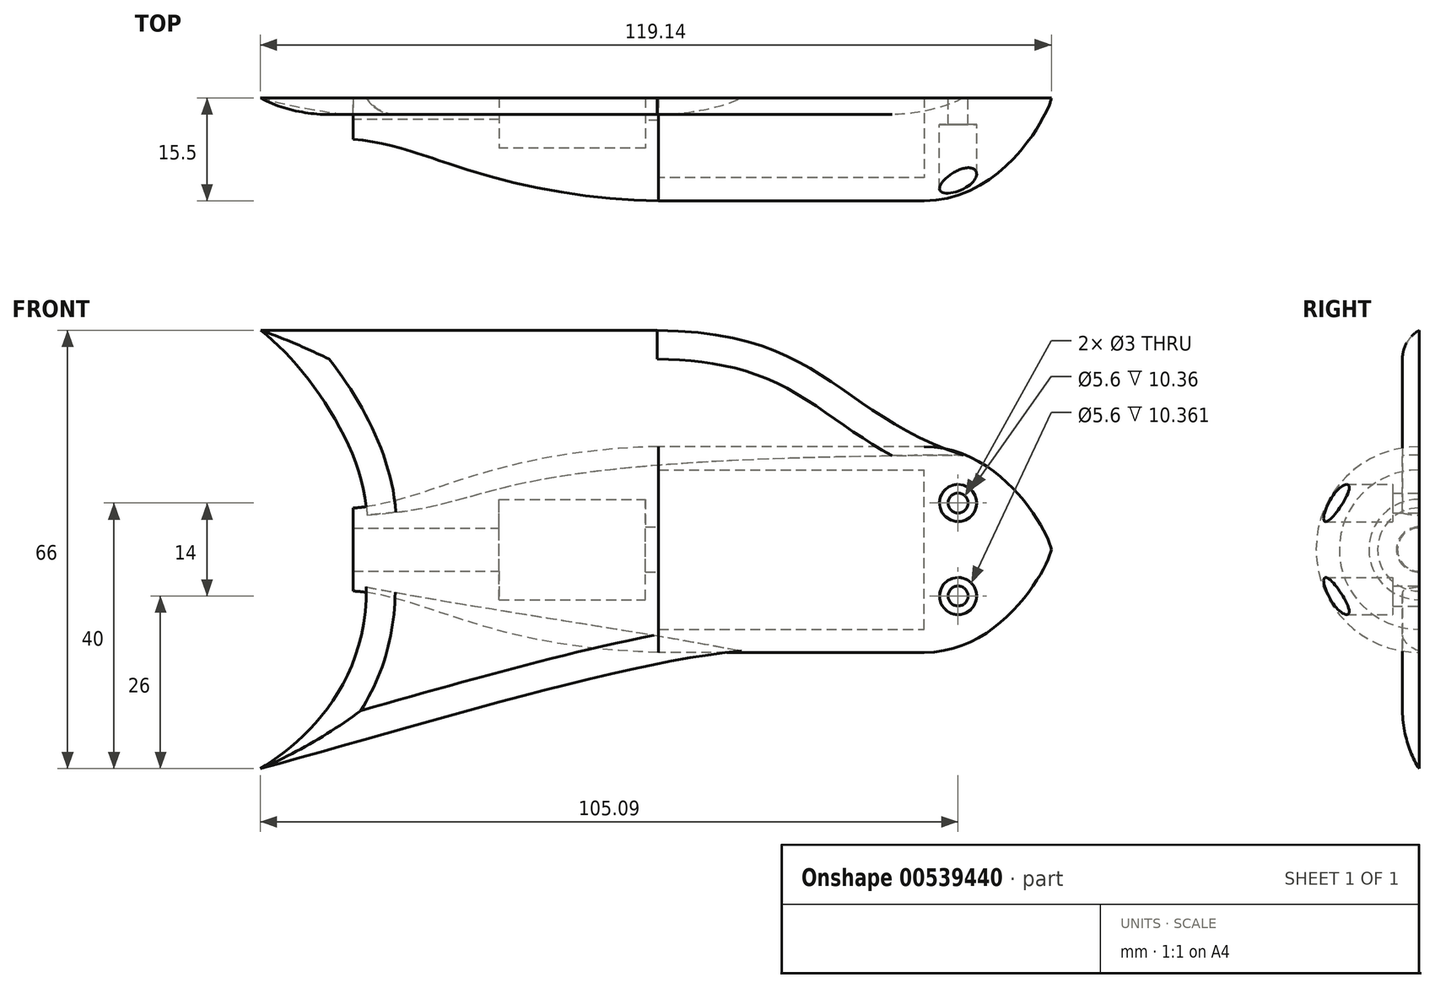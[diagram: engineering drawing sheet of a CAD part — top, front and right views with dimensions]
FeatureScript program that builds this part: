
annotation { "Feature Type Name" : "Feature", "Feature Type Description" : "" }
export const myFeature = defineFeature(function(context is Context, id is Id, definition is map)
    precondition{}
    {
        {
            var Q0;
            Q0=qCreatedBy(makeId("Front.planeOp"),FACE);
            var sketch = newSketch(context, id + "F0", { "sketchPlane" : qUnion([Q0])});
            skLineSegment(sketch, "E0", {"start": v(-75.09, 3.25) * mm, "end": v(-53.09, 3.25) * mm});
            skLineSegment(sketch, "E1", {"start": v(-53.09, 3.25) * mm, "end": v(-53.09, 7.55) * mm});
            skLineSegment(sketch, "E2", {"start": v(-53.09, 7.55) * mm, "end": v(-31.09, 7.55) * mm});
            skLineSegment(sketch, "E3", {"start": v(-31.09, 7.55) * mm, "end": v(-31.09, 3.4) * mm});
            skLineSegment(sketch, "E4", {"start": v(-31.09, 3.4) * mm, "end": v(-29.09, 3.4) * mm});
            skLineSegment(sketch, "E5", {"start": v(-29.09, 3.4) * mm, "end": v(-29.09, 12) * mm});
            skLineSegment(sketch, "E6", {"start": v(-29.09, 12) * mm, "end": v(10.91, 12) * mm});
            skLineSegment(sketch, "E7", {"start": v(10.91, 12) * mm, "end": v(10.91, 0) * mm});
            skLineSegment(sketch, "E8", {"start": v(10.91, 0) * mm, "end": v(30.05, 0) * mm});
            skLineSegment(sketch, "E9", {"start": v(-75.09, 6.25) * mm, "end": v(-75.09, 3.25) * mm});
            skLineSegment(sketch, "E10", {"start": v(10.91, 15.5) * mm, "end": v(-29.14, 15.5) * mm});
            skFitSpline(sketch, "E11", {"points": [v(30.05, 0) * mm, v(10.91, 15.5) * mm], "startDerivative": vector(-1.53, 7.93) * mm, "endDerivative": vector(-35.34, 0.06) * mm});
            skLineSegment(sketch, "E12", {"start": v(-31.09, 3.4) * mm, "end": v(-31.09, 0) * mm});
            skFitSpline(sketch, "E13", {"points": [v(-29.14, 15.5) * mm, v(-75.09, 6.25) * mm], "startDerivative": vector(-76.48, -1.84) * mm, "endDerivative": vector(-32.8, -2) * mm});
            skLineSegment(sketch, "E14", {"start": v(-53.09, 3.25) * mm, "end": v(-53.09, 0) * mm});
            skSolve(sketch);
        }
        {
            var Q0;
            Q0=makeQuery(id+"F0.imprint","IMPRINT",FACE,{"disambiguationData":[TD([[makeQuery(id+"F0.imprint","IMPRINT",EDGE,{"derivedFrom":sQuery(id+"F0.wireOp",EDGE,"E0")}),1.0]])]});
            var Q1;
            Q1=sQuery(id+"F0.wireOp",EDGE,"E8");
            revolve(context, id + "F1", {"entities" : qUnion([Q0]), "axis" : qUnion([Q1]), "revolveType" : RevolveType.ONE_DIRECTION, "angle" : 180 * degree});
        }
        {
            var Q0;
            Q0=qCreatedBy(makeId("Right.planeOp"),FACE);
            var sketch = newSketch(context, id + "F2", { "sketchPlane" : qUnion([Q0])});
            skLineSegment(sketch, "E15", {"start": v(-16.61, 2.8) * mm, "end": v(-4, 2.8) * mm});
            skLineSegment(sketch, "E16", {"start": v(-4, 2.8) * mm, "end": v(-4, 1.5) * mm});
            skLineSegment(sketch, "E17", {"start": v(-4, 1.5) * mm, "end": v(0, 1.5) * mm});
            skLineSegment(sketch, "E18", {"start": v(0, 1.5) * mm, "end": v(0, 0) * mm});
            skLineSegment(sketch, "E19", {"start": v(0, 0) * mm, "end": v(-16.61, 0) * mm});
            skLineSegment(sketch, "E20", {"start": v(-16.61, 2.8) * mm, "end": v(-16.61, 0) * mm});
            skSolve(sketch);
        }
        {
            var Q0;
            Q0=makeQuery(id+"F2.imprint","IMPRINT",FACE,{"disambiguationData":[TD([[makeQuery(id+"F2.imprint","IMPRINT",EDGE,{"derivedFrom":sQuery(id+"F2.wireOp",EDGE,"pKEryXh2-qbwp-OUbP-EK2V-zjAWTAb98PYZ")}),-1.0]])]});
            var Q1;
            Q1=makeQuery(id+"F2.imprint","IMPRINT",FACE,{"disambiguationData":[TD([[makeQuery(id+"F2.imprint","IMPRINT",EDGE,{"derivedFrom":sQuery(id+"F2.wireOp",EDGE,"E15")}),-1.0]])]});
            var Q2;
            Q2=sQuery(id+"F2.wireOp",EDGE,"E19");
            revolve(context, id + "F3", {"entities" : qUnion([Q0, Q1]), "axis" : qUnion([Q2]), "revolveType" : RevolveType.FULL});
        }
        {
            var Q0;
            Q0=makeQuery(id+"F3.opRevolve","SWEPT_BODY",BODY,{"disambiguationData":[OSD([sQuery(id+"F2.wireOp",EDGE,"E15"),sQuery(id+"F2.wireOp",EDGE,"E16"),sQuery(id+"F2.wireOp",EDGE,"E17"),sQuery(id+"F2.wireOp",EDGE,"E18"),sQuery(id+"F2.wireOp",EDGE,"E19"),sQuery(id+"F2.wireOp",EDGE,"E20")])]});
            transform(context, id + "F4", {"entities" : qUnion([Q0]), "transformType" : TransformType.TRANSLATION_3D, "dx" : 16 * mm, "dy" : 0 * mm, "dz" : 7 * mm, "makeCopy" : false});
        }
        {
            var Q0;
            Q0=makeQuery(id+"F3.opRevolve","SWEPT_BODY",BODY,{"disambiguationData":[OSD([sQuery(id+"F2.wireOp",EDGE,"E15"),sQuery(id+"F2.wireOp",EDGE,"E16"),sQuery(id+"F2.wireOp",EDGE,"E17"),sQuery(id+"F2.wireOp",EDGE,"E18"),sQuery(id+"F2.wireOp",EDGE,"E19"),sQuery(id+"F2.wireOp",EDGE,"E20")])]});
            transform(context, id + "F5", {"entities" : qUnion([Q0]), "transformType" : TransformType.TRANSLATION_3D, "dx" : 0 * mm, "dy" : 0 * mm, "dz" : -14 * mm, "makeCopy" : true});
        }
        {
            var Q0;
            Q0=makeQuery(id+"F3.opRevolve","SWEPT_BODY",BODY,{"disambiguationData":[OSD([sQuery(id+"F2.wireOp",EDGE,"E15"),sQuery(id+"F2.wireOp",EDGE,"E16"),sQuery(id+"F2.wireOp",EDGE,"E17"),sQuery(id+"F2.wireOp",EDGE,"E18"),sQuery(id+"F2.wireOp",EDGE,"E19"),sQuery(id+"F2.wireOp",EDGE,"E20")])]});
            var Q1;
            Q1=makeQuery(id+"F1.opRevolve","SWEPT_BODY",BODY,{"disambiguationData":[OSD([sQuery(id+"F0.wireOp",EDGE,"E0"),sQuery(id+"F0.wireOp",EDGE,"E1"),sQuery(id+"F0.wireOp",EDGE,"E2"),sQuery(id+"F0.wireOp",EDGE,"E3"),sQuery(id+"F0.wireOp",EDGE,"E4"),sQuery(id+"F0.wireOp",EDGE,"E5"),sQuery(id+"F0.wireOp",EDGE,"E6"),sQuery(id+"F0.wireOp",EDGE,"E7"),sQuery(id+"F0.wireOp",EDGE,"E8"),sQuery(id+"F0.wireOp",EDGE,"E9"),sQuery(id+"F0.wireOp",EDGE,"E10"),sQuery(id+"F0.wireOp",EDGE,"E11"),sQuery(id+"F0.wireOp",EDGE,"E13")])]});
            booleanBodies(context, id + "F6", {"operationType" : BooleanOperationType.SUBTRACTION, "tools" : qUnion([Q0]), "targets" : qUnion([Q1])});
        }
        {
            var Q0;
            Q0=makeQuery(id+"F5.opPattern","COPY",BODY,{"derivedFrom":makeQuery(id+"F3.opRevolve","SWEPT_BODY",BODY,{"disambiguationData":[OSD([sQuery(id+"F2.wireOp",EDGE,"E15"),sQuery(id+"F2.wireOp",EDGE,"E16"),sQuery(id+"F2.wireOp",EDGE,"E17"),sQuery(id+"F2.wireOp",EDGE,"E18"),sQuery(id+"F2.wireOp",EDGE,"E19"),sQuery(id+"F2.wireOp",EDGE,"E20")])]}),"instanceName":"1"});
            var Q1;
            Q1=makeQuery(id+"F1.opRevolve","SWEPT_BODY",BODY,{"disambiguationData":[OSD([sQuery(id+"F0.wireOp",EDGE,"E0"),sQuery(id+"F0.wireOp",EDGE,"E1"),sQuery(id+"F0.wireOp",EDGE,"E2"),sQuery(id+"F0.wireOp",EDGE,"E3"),sQuery(id+"F0.wireOp",EDGE,"E4"),sQuery(id+"F0.wireOp",EDGE,"E5"),sQuery(id+"F0.wireOp",EDGE,"E6"),sQuery(id+"F0.wireOp",EDGE,"E7"),sQuery(id+"F0.wireOp",EDGE,"E8"),sQuery(id+"F0.wireOp",EDGE,"E9"),sQuery(id+"F0.wireOp",EDGE,"E10"),sQuery(id+"F0.wireOp",EDGE,"E11"),sQuery(id+"F0.wireOp",EDGE,"E13")])]});
            booleanBodies(context, id + "F7", {"operationType" : BooleanOperationType.SUBTRACTION, "tools" : qUnion([Q0]), "targets" : qUnion([Q1])});
        }
        {
            var Q0;
            Q0=qCreatedBy(makeId("Front.planeOp"),FACE);
            var sketch = newSketch(context, id + "F8", { "sketchPlane" : qUnion([Q0])});
            skFitSpline(sketch, "E21.MirrorCS", {"points": [v(-89.1, -33) * mm, v(-73.1, -5.62) * mm], "startDerivative": vector(19.99, 12.25) * mm, "endDerivative": vector(-0.31, 44.72) * mm});
            skFitSpline(sketch, "E22.MirrorCS", {"points": [v(-73.1, -5.63) * mm, v(-16.62, -15.27) * mm], "startDerivative": vector(45.64, -9.01) * mm, "endDerivative": vector(45.64, -9.01) * mm});
            skFitSpline(sketch, "E23", {"points": [v(-16.62, -15.27) * mm, v(-89.1, -33) * mm], "startDerivative": vector(-54.11, -4.81) * mm, "endDerivative": vector(-66.28, -18) * mm});
            skSolve(sketch);
        }
        {
            var Q0;
            Q0=qCreatedBy(makeId("Front.planeOp"),FACE);
            var sketch = newSketch(context, id + "F9", { "sketchPlane" : qUnion([Q0])});
            skFitSpline(sketch, "E24", {"points": [v(-72.99, 5.2) * mm, v(16.8, 14.22) * mm], "startDerivative": vector(68.22, 4.63) * mm, "endDerivative": vector(232.35, 0.67) * mm});
            skFitSpline(sketch, "E25", {"points": [v(16.8, 14.22) * mm, v(-29.28, 33) * mm], "startDerivative": vector(-57.2, 18.37) * mm, "endDerivative": vector(-76.22, 0.95) * mm});
            skFitSpline(sketch, "E26", {"points": [v(-29.28, 33) * mm, v(-88.99, 33) * mm], "startDerivative": vector(-55.16, 0) * mm, "endDerivative": vector(-55.16, 0) * mm});
            skFitSpline(sketch, "E27", {"points": [v(-88.99, 33) * mm, v(-72.99, 5.2) * mm], "startDerivative": vector(21.07, -16.51) * mm, "endDerivative": vector(1.77, -31.08) * mm});
            skSolve(sketch);
        }
        {
            var Q0;
            Q0 = qSketchRegion(id + "F9", true);
            extrude(context, id + "F10", {"entities" : qUnion([Q0]), "depth" : 2.5 * mm, "offsetDistance" : 25 * mm});
        }
        {
            var Q0;
            Q0=makeQuery(id+"F10.opExtrude","CAP_EDGE",EDGE,{"disambiguationData":[OSD([sQuery(id+"F9.wireOp",EDGE,"E26")])],"isStart":false});
            var Q1;
            Q1=makeQuery(id+"F10.opExtrude","CAP_EDGE",EDGE,{"disambiguationData":[OSD([sQuery(id+"F9.wireOp",EDGE,"E25")])],"isStart":false});
            fillet(context, id + "F11", {"entities" : qUnion([Q0, Q1]), "radius" : 5 * mm, "tangentPropagation" : true, "allowEdgeOverflow" : false});
        }
        {
            var Q0;
            Q0=makeQuery(id+"F11.opFillet","BLEND_EDGE",EDGE,{"blendedFrom":[makeQuery(id+"F10.opExtrude","CAP_EDGE",EDGE,{"disambiguationData":[OSD([sQuery(id+"F9.wireOp",EDGE,"E26")])],"isStart":false}),makeQuery(id+"F10.opExtrude","SWEPT_FACE",FACE,{"disambiguationData":[OSD([sQuery(id+"F9.wireOp",EDGE,"E27")])]})],"blendedInto":[makeQuery(id+"F10.opExtrude","SWEPT_FACE",FACE,{"disambiguationData":[OSD([sQuery(id+"F9.wireOp",EDGE,"E27")])]})]});
            fillet(context, id + "F12", {"entities" : qUnion([Q0]), "radius" : 5 * mm, "tangentPropagation" : true, "allowEdgeOverflow" : false});
        }
        {
            var Q0;
            Q0=makeQuery(id+"F8.imprint","IMPRINT",FACE,{"disambiguationData":[TD([[makeQuery(id+"F8.imprint","IMPRINT",EDGE,{"derivedFrom":sQuery(id+"F8.wireOp",EDGE,"E21.MirrorCS")}),-1.0]])]});
            extrude(context, id + "F13", {"entities" : qUnion([Q0]), "depth" : 2.5 * mm, "offsetDistance" : 25 * mm});
        }
        {
            var Q0;
            Q0=makeQuery(id+"F13.opExtrude","CAP_EDGE",EDGE,{"disambiguationData":[OSD([sQuery(id+"F8.wireOp",EDGE,"E21.MirrorCS")])],"isStart":false});
            fillet(context, id + "F14", {"entities" : qUnion([Q0]), "radius" : 5 * mm, "tangentPropagation" : true, "allowEdgeOverflow" : false});
        }
        {
            var Q0;
            Q0=makeQuery(id+"F13.opExtrude","CAP_EDGE",EDGE,{"disambiguationData":[OSD([sQuery(id+"F8.wireOp",EDGE,"E23")])],"isStart":false});
            fillet(context, id + "F15", {"entities" : qUnion([Q0]), "radius" : 5 * mm, "tangentPropagation" : true, "allowEdgeOverflow" : false});
        }
    });
